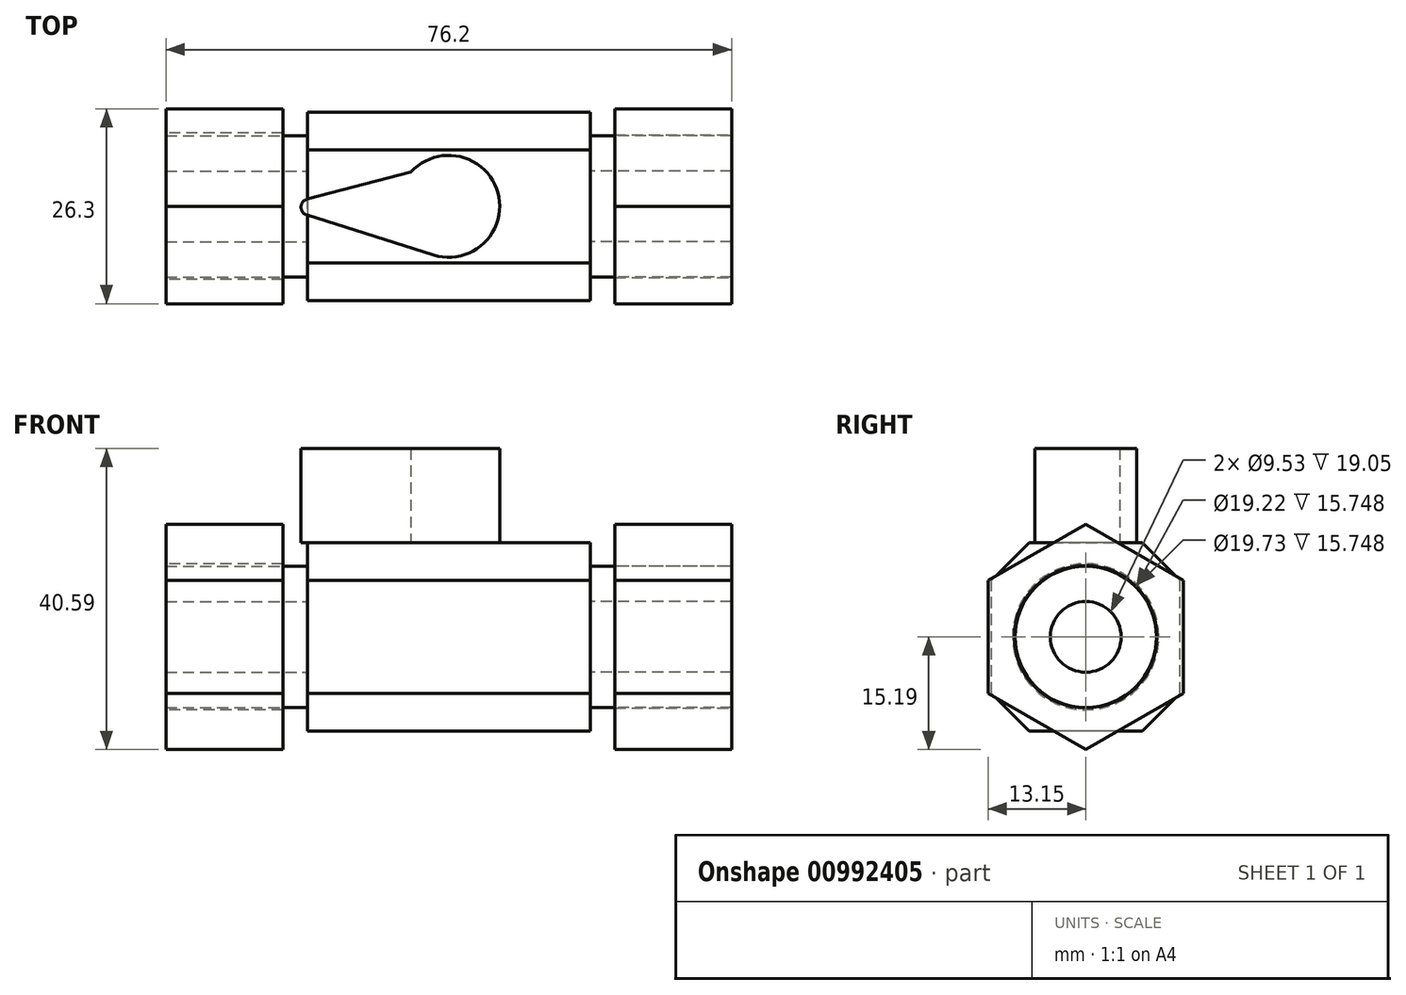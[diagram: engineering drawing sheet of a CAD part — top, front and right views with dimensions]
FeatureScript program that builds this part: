
annotation { "Feature Type Name" : "Feature", "Feature Type Description" : "" }
export const myFeature = defineFeature(function(context is Context, id is Id, definition is map)
    precondition{}
    {
        {
            var Q0;
            Q0=qCreatedBy(makeId("Right.planeOp"),FACE);
            var sketch = newSketch(context, id + "F0", { "sketchPlane" : qUnion([Q0])});
            skLineSegment(sketch, "E0.bottom", {"start": v(12.7, -12.7) * mm, "end": v(-12.7, -12.7) * mm});
            skLineSegment(sketch, "E0.top", {"start": v(12.7, 12.7) * mm, "end": v(-12.7, 12.7) * mm});
            skLineSegment(sketch, "E0.left", {"start": v(12.7, -12.7) * mm, "end": v(12.7, 12.7) * mm});
            skLineSegment(sketch, "E0.right", {"start": v(-12.7, -12.7) * mm, "end": v(-12.7, 12.7) * mm});
            skPoint(sketch, "E0.middle", {"position": v(0, 0) * mm});
            skSolve(sketch);
        }
        {
            var Q0;
            Q0 = qSketchRegion(id + "F0", true);
            extrude(context, id + "F1", {"entities" : qUnion([Q0]), "depth" : 38.1 * mm, "offsetDistance" : 25.4 * mm, "symmetric" : true});
        }
        {
            var Q0;
            Q0=makeQuery(id+"F1.opExtrude","CAP_FACE",FACE,{"disambiguationData":[OSD([sQuery(id+"F0.wireOp",EDGE,"E0.bottom"),sQuery(id+"F0.wireOp",EDGE,"E0.top"),sQuery(id+"F0.wireOp",EDGE,"E0.left"),sQuery(id+"F0.wireOp",EDGE,"E0.right")])],"isStart":false});
            var sketch = newSketch(context, id + "F2", { "sketchPlane" : qUnion([Q0])});
            skCircle(sketch, "E1", {"center": v(0, 0) * mm, "radius": 9.53 * mm});
            skCircle(sketch, "E2", {"center": v(0, 0) * mm, "radius": 4.76 * mm});
            skSolve(sketch);
        }
        {
            var Q0;
            Q0 = qSketchRegion(id + "F2", true);
            extrude(context, id + "F3", {"entities" : qUnion([Q0]), "operationType" : NewBodyOperationType.ADD, "depth" : 19.05 * mm, "offsetDistance" : 25.4 * mm});
        }
        {
            var Q0;
            Q0=makeQuery(id+"F1.opExtrude","CAP_FACE",FACE,{"disambiguationData":[OSD([sQuery(id+"F0.wireOp",EDGE,"E0.bottom"),sQuery(id+"F0.wireOp",EDGE,"E0.top"),sQuery(id+"F0.wireOp",EDGE,"E0.left"),sQuery(id+"F0.wireOp",EDGE,"E0.right")])],"isStart":true});
            var sketch = newSketch(context, id + "F4", { "sketchPlane" : qUnion([Q0])});
            skCircle(sketch, "E3", {"center": v(0, 0) * mm, "radius": 9.53 * mm});
            skCircle(sketch, "E4", {"center": v(0, 0) * mm, "radius": 4.76 * mm});
            skSolve(sketch);
        }
        {
            var Q0;
            Q0 = qSketchRegion(id + "F4", true);
            extrude(context, id + "F5", {"entities" : qUnion([Q0]), "operationType" : NewBodyOperationType.ADD, "depth" : 19.05 * mm, "offsetDistance" : 25.4 * mm});
        }
        {
            var Q0;
            Q0=makeQuery(id+"F5.opExtrude","CAP_FACE",FACE,{"disambiguationData":[OSD([sQuery(id+"F4.wireOp",EDGE,"E3"),sQuery(id+"F4.wireOp",EDGE,"E4")])],"isStart":false});
            var sketch = newSketch(context, id + "F6", { "sketchPlane" : qUnion([Q0])});
            skCircle(sketch, "E5.cCircle", {"center": v(0, 0) * mm, "radius": 13.15 * mm, "construction": true});
            skLineSegment(sketch, "E5.0", {"start": v(13.15, 7.6) * mm, "end": v(13.15, -7.6) * mm});
            skLineSegment(sketch, "E5.1", {"start": v(13.15, -7.6) * mm, "end": v(0, -15.19) * mm});
            skLineSegment(sketch, "E5.2", {"start": v(0, -15.19) * mm, "end": v(-13.15, -7.6) * mm});
            skLineSegment(sketch, "E5.3", {"start": v(-13.15, -7.6) * mm, "end": v(-13.15, 7.6) * mm});
            skLineSegment(sketch, "E5.4", {"start": v(-13.15, 7.6) * mm, "end": v(0, 15.19) * mm});
            skLineSegment(sketch, "E5.5", {"start": v(0, 15.19) * mm, "end": v(13.15, 7.6) * mm});
            skPoint(sketch, "E5.0.midPoint", {"position": v(13.15, 0) * mm});
            skCircle(sketch, "E6", {"center": v(0, 0) * mm, "radius": 9.86 * mm});
            skSolve(sketch);
        }
        {
            var Q0;
            Q0 = qSketchRegion(id + "F6", true);
            extrude(context, id + "F7", {"entities" : qUnion([Q0]), "oppositeDirection" : true, "depth" : 15.75 * mm, "offsetDistance" : 25.4 * mm});
        }
        {
            var Q0;
            Q0=makeQuery(id+"F3.opExtrude","CAP_FACE",FACE,{"disambiguationData":[OSD([sQuery(id+"F2.wireOp",EDGE,"E1"),sQuery(id+"F2.wireOp",EDGE,"E2")])],"isStart":false});
            var sketch = newSketch(context, id + "F8", { "sketchPlane" : qUnion([Q0])});
            skCircle(sketch, "E7.cCircle", {"center": v(0, 0) * mm, "radius": 13.15 * mm, "construction": true});
            skLineSegment(sketch, "E7.0", {"start": v(13.15, 7.6) * mm, "end": v(13.15, -7.6) * mm});
            skLineSegment(sketch, "E7.1", {"start": v(13.15, -7.6) * mm, "end": v(0, -15.19) * mm});
            skLineSegment(sketch, "E7.2", {"start": v(0, -15.19) * mm, "end": v(-13.15, -7.6) * mm});
            skLineSegment(sketch, "E7.3", {"start": v(-13.15, -7.6) * mm, "end": v(-13.15, 7.6) * mm});
            skLineSegment(sketch, "E7.4", {"start": v(-13.15, 7.6) * mm, "end": v(0, 15.19) * mm});
            skLineSegment(sketch, "E7.5", {"start": v(0, 15.19) * mm, "end": v(13.15, 7.6) * mm});
            skPoint(sketch, "E7.0.midPoint", {"position": v(13.15, 0) * mm});
            skCircle(sketch, "E8", {"center": v(0, 0) * mm, "radius": 9.61 * mm});
            skSolve(sketch);
        }
        {
            var Q0;
            Q0 = qSketchRegion(id + "F8", true);
            extrude(context, id + "F9", {"entities" : qUnion([Q0]), "oppositeDirection" : true, "depth" : 15.75 * mm, "offsetDistance" : 25.4 * mm});
        }
        {
            var Q0;
            Q0=makeQuery(id+"F1.opExtrude","SWEPT_EDGE",EDGE,{"disambiguationData":[OSD([sQuery(id+"F0.wireOp",EDGE,"E0.top"),sQuery(id+"F0.wireOp",EDGE,"E0.left")])]});
            var Q1;
            Q1=makeQuery(id+"F1.opExtrude","SWEPT_EDGE",EDGE,{"disambiguationData":[OSD([sQuery(id+"F0.wireOp",EDGE,"E0.bottom"),sQuery(id+"F0.wireOp",EDGE,"E0.left")])]});
            var Q2;
            Q2=makeQuery(id+"F1.opExtrude","SWEPT_EDGE",EDGE,{"disambiguationData":[OSD([sQuery(id+"F0.wireOp",EDGE,"E0.top"),sQuery(id+"F0.wireOp",EDGE,"E0.right")])]});
            var Q3;
            Q3=makeQuery(id+"F1.opExtrude","SWEPT_EDGE",EDGE,{"disambiguationData":[OSD([sQuery(id+"F0.wireOp",EDGE,"E0.bottom"),sQuery(id+"F0.wireOp",EDGE,"E0.right")])]});
            chamfer(context, id + "F10", {"entities" : qUnion([Q0, Q1, Q2, Q3]), "width" : 5.08 * mm, "tangentPropagation" : true});
        }
        {
            var Q0;
            Q0=makeQuery(id+"F1.opExtrude","SWEPT_FACE",FACE,{"disambiguationData":[OSD([sQuery(id+"F0.wireOp",EDGE,"E0.top")])]});
            var sketch = newSketch(context, id + "F11", { "sketchPlane" : qUnion([Q0])});
            skCircle(sketch, "E9", {"center": v(0, 0) * mm, "radius": 6.87 * mm});
            skLineSegment(sketch, "E10", {"start": v(-5.11, 4.6) * mm, "end": v(-19.05, 0.98) * mm});
            skLineSegment(sketch, "E11", {"start": v(-19.1, -1.18) * mm, "end": v(-2.07, -6.55) * mm});
            skPoint(sketch, "E12.visualSharp", {"position": v(-22.85, 0) * mm});
            skArc(sketch, "E12.filletArc", {"start": v(-19.05, 0.98) * mm, "mid": v(-19.9, -0.08) * mm, "end": v(-19.1, -1.18) * mm});
            skSolve(sketch);
        }
        {
            var Q0;
            Q0 = qSketchRegion(id + "F11", true);
            extrude(context, id + "F12", {"entities" : qUnion([Q0]), "depth" : 12.7 * mm, "offsetDistance" : 25.4 * mm});
        }
    });
